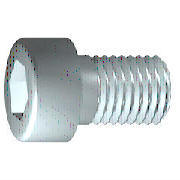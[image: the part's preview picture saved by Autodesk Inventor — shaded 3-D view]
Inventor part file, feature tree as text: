
AUTODESK INVENTOR PART (.ipt)
format: ipt  version: 2022 (Build 260153000, 153)  size: 191,488 bytes
history: native  units: mm (DEFAULTED — no unit token found)
features: sketch x2, other x1, extrude x1, plane x1, fillet x1
ambient origin geometry x7: Origin, YZ Plane, XY Plane, X Axis, Y Axis, Z Axis, Center Point
bodies: Solid1 (feature_tree)
feature tree (6):
  other  "Базовый элемент"
  extrude  "Паз"  Depth=8.875mm
  plane  "Work Plane1"
  fillet  "Fillet2"  Radius=0.276153mm
  sketch  "Эскиз1"
  sketch  "Эскиз2"
